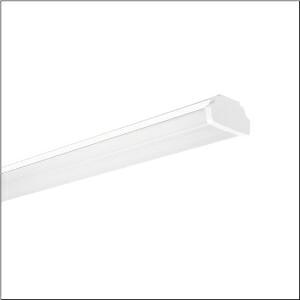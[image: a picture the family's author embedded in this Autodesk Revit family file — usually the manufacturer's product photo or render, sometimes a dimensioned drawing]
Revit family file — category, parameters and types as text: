
# Revit family: modario_r__31_gen_2_53bm812dv6a5c2_a7ef
name_source: partatom
category: Lighting Fixtures
units: mm (PartAtom-declared; Revit-internal decimal feet)

## family parameters
Cut with Voids When Loaded = No
Host = Face
Light Source = No
Part Type = Normal
Room Calculation Point = No
Round Connector Dimension = Use Diameter
Shared = No

## types (1)
- --- (1 x LED, 10550 lm, 61.4 W, 6500K)
    Apparent Load = 61 VA
    CIE Flux Codes = 47 80 95 93 100
    Color Rendering = 80
    Color Temperature = 6500K
    Default Elevation = 1800 mm
    Description = Modario® 31 Gen.2, luminaire insert, of sheet steel, coil coated, white, length: 1.495mm, width: 81mm, height: 82mm, 5x system unit, system units: 299mm, LED rated luminous flux: 10.550lm, light colour: 865, control gear: DALI 2, control gear: ECG DALI, with plug, 5-pole, with phase selection, mains connection: 220..240V, AC, 50/60Hz, rated input power: 61W, through-wiring accessed according to module size, primary optical cover: cover, of PMMA, light emission: direct distribution, primary light characteristic: symmetric, protection rating (complete): IP20, protection rating (LED compartment): IP50, insulation class (complete): insulation class I (protective earthing), certification: CE, ENEC, VDE, UKCA, impact resistance: IK03, permissible ambient temperature for indoor applications: -25..+35°C, corresponds to IFS (International Featured Standards) requirements for safety and quality in the food industry, reducing of maximum allowable ambient temperature of 5°C with ceiling mounting, IP40 when using the optional accessory 5TP9018, packaging unit: 1 piece
    Height = 92 mm
    Lamp = 1 x LED
    Lamp Light Flux = 10550 lm
    Lamp Power = 61.4 W
    Lamp count = 1
    Length = 1495 mm
    Luminous efficacy = 172 lm/W
    Manufacturer = Siteco
    ModVariant = No
    Model = 53BM812DV6A5C2
    Mounting Place = Ceiling
    Mounting Type = Pendant
    Number of Poles = 1
    OnlyDefault = Yes
    Power Factor = 1
    Product Name = Modario® 31 Gen.2
    Product group = luminaire insert
    ProductGroupID = 901
    Protection Class = Protection class I
    Protection Degree = IP 20
    RLX_Detail_Level = 1
    RLX_Emergency_Light_Flux = 0 lm
    RLX_Emergency_Type = 0
    RLX_Emergency_Type_DB = No
    RlxData = <blob elided: 42277 chars, md5=d85801cb>
    Socket = socket
    Standby Power = 0 W
    System Light Flux = 10550 lm
    System Power = 61 W
    Type Comments = factory setting: luminous flux: 100 % | dim-lin: 254 | 418 mA
    Type Image = l_1319597.jpg
    URL = http://relux.com
    VarID = @adj_010841
    Voltage = 0 V
    Weight = 0.00 kg
    Width = 81 mm

## geometry (parser evidence)
native form markers: Blend x4, Sweep x14
no freeform markers — native parametric forms only
